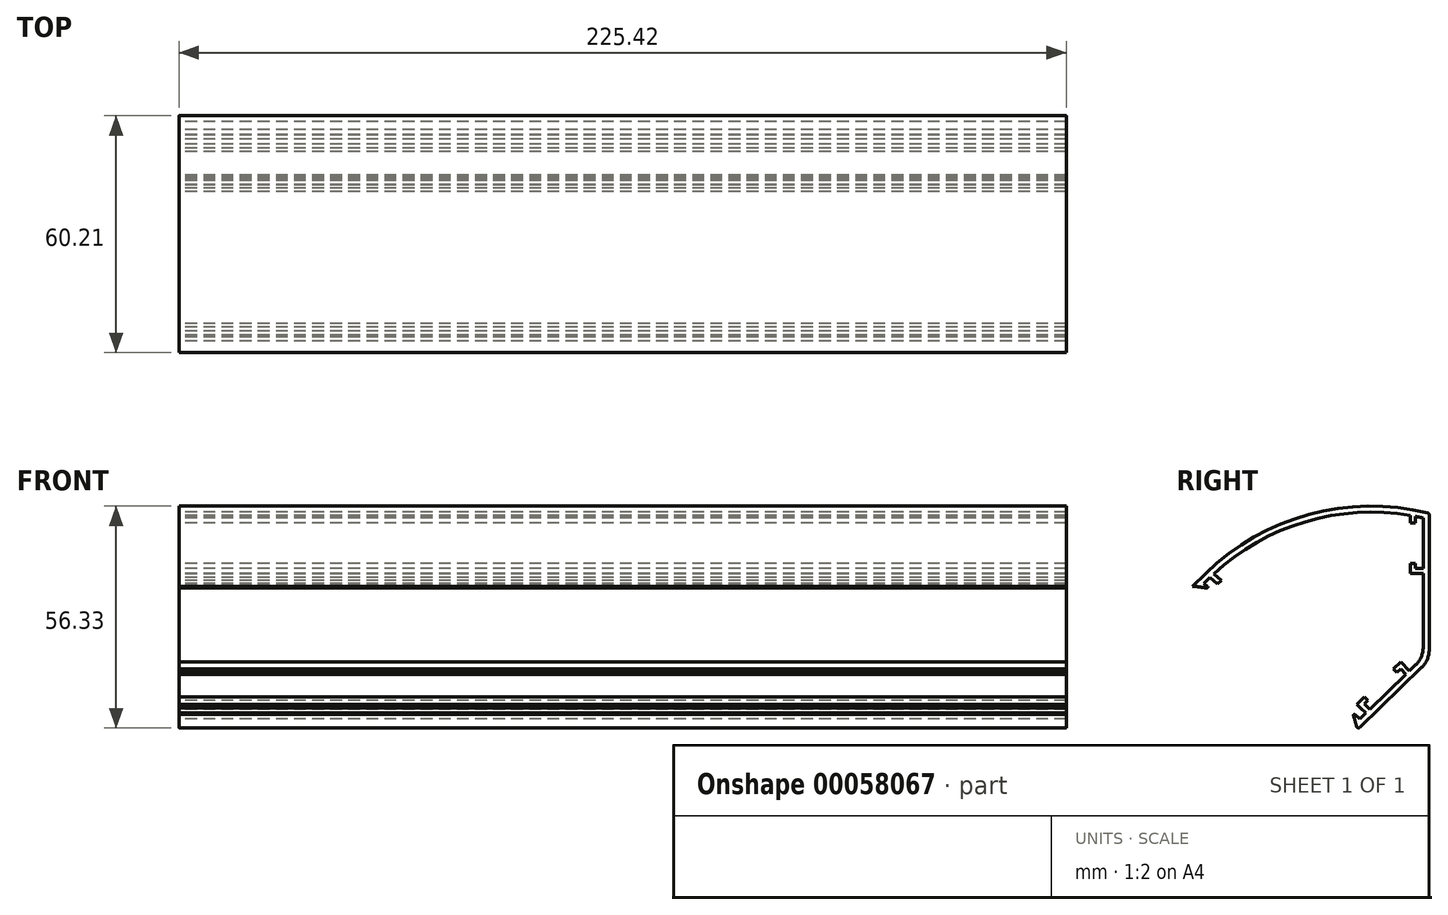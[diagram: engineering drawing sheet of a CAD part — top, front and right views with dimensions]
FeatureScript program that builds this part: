
annotation { "Feature Type Name" : "Feature", "Feature Type Description" : "" }
export const myFeature = defineFeature(function(context is Context, id is Id, definition is map)
    precondition{}
    {
        {
            var Q0;
            Q0=qCreatedBy(makeId("Right.planeOp"),FACE);
            var sketch = newSketch(context, id + "F0", { "sketchPlane" : qUnion([Q0])});
            skLineSegment(sketch, "E0", {"start": v(-18.27, -17.64) * mm, "end": v(0, 0) * mm});
            skLineSegment(sketch, "E1", {"start": v(0, 0) * mm, "end": v(0, 37.34) * mm});
            skArc(sketch, "E2", {"start": v(0, 37.34) * mm, "mid": v(-30.37, 37.1) * mm, "end": v(-56.79, 22.12) * mm});
            skLineSegment(sketch, "E3", {"start": v(-56.79, 22.12) * mm, "end": v(-60.2, 18.8) * mm});
            skLineSegment(sketch, "E4", {"start": v(-18.27, -17.64) * mm, "end": v(-60.2, 18.8) * mm});
            skLineSegment(sketch, "E5", {"start": v(-56.79, 22.12) * mm, "end": v(-18.27, -17.64) * mm, "construction": true});
            skLineSegment(sketch, "E6", {"start": v(0, 37.34) * mm, "end": v(-56.79, 22.12) * mm, "construction": true});
            skSolve(sketch);
        }
        {
            var Q0;
            Q0=qSketchRegion(id+"F0",true);
            extrude(context, id + "F1", {"entities" : qUnion([Q0]), "endBound" : BoundingType.SYMMETRIC, "depth" : 225.42 * mm});
        }
        {
            var Q0;
            Q0=makeQuery(id+"F1.opExtrude","SWEPT_FACE",FACE,{"disambiguationData":[OSD([sQuery(id+"F0.wireOp",EDGE,"E4")])]});
            var Q1;
            Q1=makeQuery(id+"F1.opExtrude","CAP_FACE",FACE,{"disambiguationData":[OSD([sQuery(id+"F0.wireOp",EDGE,"E0"),sQuery(id+"F0.wireOp",EDGE,"E1"),sQuery(id+"F0.wireOp",EDGE,"E2"),sQuery(id+"F0.wireOp",EDGE,"E3"),sQuery(id+"F0.wireOp",EDGE,"E4")])],"isStart":true});
            var Q2;
            Q2=makeQuery(id+"F1.opExtrude","CAP_FACE",FACE,{"disambiguationData":[OSD([sQuery(id+"F0.wireOp",EDGE,"E0"),sQuery(id+"F0.wireOp",EDGE,"E1"),sQuery(id+"F0.wireOp",EDGE,"E2"),sQuery(id+"F0.wireOp",EDGE,"E3"),sQuery(id+"F0.wireOp",EDGE,"E4")])],"isStart":false});
            shell(context, id + "F2", {"entities" : qUnion([Q0, Q1, Q2]), "thickness" : 1.52 * mm});
        }
        {
            var Q0;
            Q0=makeQuery(id+"F1.opExtrude","CAP_FACE",FACE,{"disambiguationData":[OSD([sQuery(id+"F0.wireOp",EDGE,"E0"),sQuery(id+"F0.wireOp",EDGE,"E1"),sQuery(id+"F0.wireOp",EDGE,"E2"),sQuery(id+"F0.wireOp",EDGE,"E3"),sQuery(id+"F0.wireOp",EDGE,"E4")])],"isStart":true});
            var sketch = newSketch(context, id + "F3", { "sketchPlane" : qUnion([Q0])});
            skLineSegment(sketch, "E7", {"start": v(60.2, 18.8) * mm, "end": v(18.27, -17.64) * mm, "construction": true});
            skSolve(sketch);
        }
        {
            var Q0;
            {var subQ6=sQuery(id+"F0.wireOp",EDGE,"E0");var subQ7=makeQuery(id+"F1.opExtrude","CAP_EDGE",EDGE,{"disambiguationData":[OSD([subQ6])],"isStart":true});Q0=makeQuery(id+"F3.imprint","IMPRINT",FACE,{"disambiguationData":[TD([[makeQuery(id+"F3.imprint","IMPRINT",EDGE,{"derivedFrom":subQ7}),-1.0]])]});}
            var sketch = newSketch(context, id + "F4", { "sketchPlane" : qUnion([Q0])});
            skLineSegment(sketch, "E8", {"start": v(59.05, 17.8) * mm, "end": v(57.23, 19.57) * mm});
            skLineSegment(sketch, "E9", {"start": v(57.23, 19.57) * mm, "end": v(55.31, 17.9) * mm});
            skLineSegment(sketch, "E10", {"start": v(55.31, 17.9) * mm, "end": v(57.13, 16.14) * mm});
            skLineSegment(sketch, "E11", {"start": v(57.13, 16.14) * mm, "end": v(59.05, 17.8) * mm});
            skSolve(sketch);
        }
        {
            var Q0;
            Q0=qSketchRegion(id+"F4",true);
            var Q1;
            Q1=makeQuery(id+"F1.opExtrude","CAP_FACE",FACE,{"disambiguationData":[OSD([sQuery(id+"F0.wireOp",EDGE,"E0"),sQuery(id+"F0.wireOp",EDGE,"E1"),sQuery(id+"F0.wireOp",EDGE,"E2"),sQuery(id+"F0.wireOp",EDGE,"E3"),sQuery(id+"F0.wireOp",EDGE,"E4")])],"isStart":false});
            extrude(context, id + "F5", {"entities" : qUnion([Q0]), "operationType" : NewBodyOperationType.ADD, "endBound" : BoundingType.UP_TO_SURFACE, "oppositeDirection" : true, "endBoundEntityFace" : qUnion([Q1]), "depth" : 25.4 * mm});
        }
        {
            var Q0;
            {var subQ6=sQuery(id+"F0.wireOp",EDGE,"E0");var subQ7=makeQuery(id+"F1.opExtrude","CAP_EDGE",EDGE,{"disambiguationData":[OSD([subQ6])],"isStart":true});Q0=makeQuery(id+"F3.imprint","IMPRINT",FACE,{"disambiguationData":[TD([[makeQuery(id+"F3.imprint","IMPRINT",EDGE,{"derivedFrom":subQ7}),-1.0]])]});}
            var sketch = newSketch(context, id + "F6", { "sketchPlane" : qUnion([Q0])});
            skLineSegment(sketch, "E12", {"start": v(17.6, -14.88) * mm, "end": v(19.43, -16.64) * mm});
            skLineSegment(sketch, "E13", {"start": v(19.43, -16.64) * mm, "end": v(21.34, -14.97) * mm});
            skLineSegment(sketch, "E14", {"start": v(21.34, -14.97) * mm, "end": v(19.52, -13.2) * mm});
            skLineSegment(sketch, "E15", {"start": v(19.52, -13.2) * mm, "end": v(17.6, -14.88) * mm});
            skSolve(sketch);
        }
        {
            var Q0;
            Q0=qSketchRegion(id+"F6",true);
            var Q1;
            Q1=makeQuery(id+"F5.boolean.opBoolean","MERGE",FACE,{"derivedFrom":[makeQuery(id+"F1.opExtrude","CAP_FACE",FACE,{"disambiguationData":[OSD([sQuery(id+"F0.wireOp",EDGE,"E0"),sQuery(id+"F0.wireOp",EDGE,"E1"),sQuery(id+"F0.wireOp",EDGE,"E2"),sQuery(id+"F0.wireOp",EDGE,"E3"),sQuery(id+"F0.wireOp",EDGE,"E4")])],"isStart":false}),makeQuery(id+"F5.opExtrude","CAP_FACE",FACE,{"disambiguationData":[OSD([sQuery(id+"F4.wireOp",EDGE,"E8"),sQuery(id+"F4.wireOp",EDGE,"E9"),sQuery(id+"F4.wireOp",EDGE,"E10"),sQuery(id+"F4.wireOp",EDGE,"E11")])],"isStart":false})]});
            extrude(context, id + "F7", {"entities" : qUnion([Q0]), "operationType" : NewBodyOperationType.ADD, "endBound" : BoundingType.UP_TO_SURFACE, "oppositeDirection" : true, "endBoundEntityFace" : qUnion([Q1]), "depth" : 25.4 * mm});
        }
        {
            var Q0;
            {var subQ6=sQuery(id+"F0.wireOp",EDGE,"E0");var subQ7=makeQuery(id+"F1.opExtrude","CAP_EDGE",EDGE,{"disambiguationData":[OSD([subQ6])],"isStart":true});Q0=makeQuery(id+"F3.imprint","IMPRINT",FACE,{"disambiguationData":[TD([[makeQuery(id+"F3.imprint","IMPRINT",EDGE,{"derivedFrom":subQ7}),-1.0]])]});}
            var sketch = newSketch(context, id + "F8", { "sketchPlane" : qUnion([Q0])});
            skCircle(sketch, "E16", {"center": v(64.21, -28.14) * mm, "radius": 47.12 * mm});
            skSolve(sketch);
        }
        {
            var Q0;
            Q0=qSketchRegion(id+"F8",true);
            var Q1;
            Q1=makeQuery(id+"F7.boolean.opBoolean","MERGE",FACE,{"derivedFrom":[makeQuery(id+"F5.boolean.opBoolean","MERGE",FACE,{"derivedFrom":[makeQuery(id+"F1.opExtrude","CAP_FACE",FACE,{"disambiguationData":[OSD([sQuery(id+"F0.wireOp",EDGE,"E0"),sQuery(id+"F0.wireOp",EDGE,"E1"),sQuery(id+"F0.wireOp",EDGE,"E2"),sQuery(id+"F0.wireOp",EDGE,"E3"),sQuery(id+"F0.wireOp",EDGE,"E4")])],"isStart":false}),makeQuery(id+"F5.opExtrude","CAP_FACE",FACE,{"disambiguationData":[OSD([sQuery(id+"F4.wireOp",EDGE,"E8"),sQuery(id+"F4.wireOp",EDGE,"E9"),sQuery(id+"F4.wireOp",EDGE,"E10"),sQuery(id+"F4.wireOp",EDGE,"E11")])],"isStart":false})]}),makeQuery(id+"F7.opExtrude","CAP_FACE",FACE,{"disambiguationData":[OSD([sQuery(id+"F6.wireOp",EDGE,"E12"),sQuery(id+"F6.wireOp",EDGE,"E13"),sQuery(id+"F6.wireOp",EDGE,"E14"),sQuery(id+"F6.wireOp",EDGE,"E15")])],"isStart":false})]});
            extrude(context, id + "F9", {"entities" : qUnion([Q0]), "operationType" : NewBodyOperationType.REMOVE, "endBound" : BoundingType.UP_TO_SURFACE, "oppositeDirection" : true, "endBoundEntityFace" : qUnion([Q1]), "depth" : 25.4 * mm});
        }
        {
            var Q0;
            {var subQ6=sQuery(id+"F0.wireOp",EDGE,"E0");var subQ7=makeQuery(id+"F1.opExtrude","CAP_EDGE",EDGE,{"disambiguationData":[OSD([subQ6])],"isStart":true});Q0=makeQuery(id+"F3.imprint","IMPRINT",FACE,{"disambiguationData":[TD([[makeQuery(id+"F3.imprint","IMPRINT",EDGE,{"derivedFrom":subQ7}),-1.0]])]});}
            var sketch = newSketch(context, id + "F10", { "sketchPlane" : qUnion([Q0])});
            skLineSegment(sketch, "E17", {"start": v(16.05, -13.38) * mm, "end": v(17.53, -12.09) * mm});
            skLineSegment(sketch, "E18", {"start": v(17.53, -12.09) * mm, "end": v(16.5, -11.09) * mm});
            skLineSegment(sketch, "E19", {"start": v(16.5, -11.09) * mm, "end": v(15.13, -12.5) * mm});
            skLineSegment(sketch, "E20", {"start": v(15.13, -12.5) * mm, "end": v(16.05, -13.38) * mm});
            skSolve(sketch);
        }
        {
            var Q0;
            {var subQ6=sQuery(id+"F0.wireOp",EDGE,"E0");var subQ7=makeQuery(id+"F1.opExtrude","CAP_EDGE",EDGE,{"disambiguationData":[OSD([subQ6])],"isStart":true});Q0=makeQuery(id+"F3.imprint","IMPRINT",FACE,{"disambiguationData":[TD([[makeQuery(id+"F3.imprint","IMPRINT",EDGE,{"derivedFrom":subQ7}),-1.0]])]});}
            var sketch = newSketch(context, id + "F11", { "sketchPlane" : qUnion([Q0])});
            skLineSegment(sketch, "E21", {"start": v(17.53, -12.09) * mm, "end": v(15.58, -10.2) * mm});
            skLineSegment(sketch, "E22", {"start": v(15.58, -10.2) * mm, "end": v(16.46, -9.3) * mm});
            skLineSegment(sketch, "E23", {"start": v(16.46, -9.3) * mm, "end": v(18.4, -11.17) * mm});
            skLineSegment(sketch, "E24", {"start": v(18.4, -11.17) * mm, "end": v(17.53, -12.09) * mm});
            skSolve(sketch);
        }
        {
            var Q0;
            {var subQ6=sQuery(id+"F0.wireOp",EDGE,"E0");var subQ7=makeQuery(id+"F1.opExtrude","CAP_EDGE",EDGE,{"disambiguationData":[OSD([subQ6])],"isStart":true});Q0=makeQuery(id+"F3.imprint","IMPRINT",FACE,{"disambiguationData":[TD([[makeQuery(id+"F3.imprint","IMPRINT",EDGE,{"derivedFrom":subQ7}),-1.0]])]});}
            var sketch = newSketch(context, id + "F12", { "sketchPlane" : qUnion([Q0])});
            skLineSegment(sketch, "E25", {"start": v(55.68, 21.07) * mm, "end": v(53.76, 19.4) * mm});
            skLineSegment(sketch, "E26", {"start": v(53.76, 19.4) * mm, "end": v(52.85, 20.3) * mm});
            skLineSegment(sketch, "E27", {"start": v(52.85, 20.3) * mm, "end": v(54.76, 21.96) * mm});
            skLineSegment(sketch, "E28", {"start": v(54.76, 21.96) * mm, "end": v(55.68, 21.07) * mm});
            skSolve(sketch);
        }
        {
            var Q0;
            {var subQ6=sQuery(id+"F0.wireOp",EDGE,"E0");var subQ7=makeQuery(id+"F1.opExtrude","CAP_EDGE",EDGE,{"disambiguationData":[OSD([subQ6])],"isStart":true});Q0=makeQuery(id+"F3.imprint","IMPRINT",FACE,{"disambiguationData":[TD([[makeQuery(id+"F3.imprint","IMPRINT",EDGE,{"derivedFrom":subQ7}),-1.0]])]});}
            var sketch = newSketch(context, id + "F13", { "sketchPlane" : qUnion([Q0])});
            skLineSegment(sketch, "E29", {"start": v(5.9, -3.58) * mm, "end": v(7.26, -2.18) * mm});
            skLineSegment(sketch, "E30", {"start": v(7.26, -2.18) * mm, "end": v(8.18, -3.06) * mm});
            skLineSegment(sketch, "E31", {"start": v(8.18, -3.06) * mm, "end": v(9.06, -2.15) * mm});
            skLineSegment(sketch, "E32", {"start": v(9.06, -2.15) * mm, "end": v(7.23, -0.38) * mm});
            skLineSegment(sketch, "E33", {"start": v(7.23, -0.38) * mm, "end": v(5, -2.7) * mm});
            skLineSegment(sketch, "E34", {"start": v(5, -2.7) * mm, "end": v(5.9, -3.58) * mm});
            skSolve(sketch);
        }
        {
            var Q0;
            {var subQ6=sQuery(id+"F12.wireOp",EDGE,"E28");Q0=makeQuery(id+"F12.imprint","IMPRINT",FACE,{"disambiguationData":[TD([[makeQuery(id+"F12.imprint","IMPRINT",EDGE,{"derivedFrom":subQ6}),1.0]])]});}
            var sketch = newSketch(context, id + "F14", { "sketchPlane" : qUnion([Q0])});
            skLineSegment(sketch, "E35", {"start": v(1.52, 22.04) * mm, "end": v(1.52, 23.3) * mm});
            skLineSegment(sketch, "E36", {"start": v(1.52, 23.3) * mm, "end": v(3.48, 23.3) * mm});
            skLineSegment(sketch, "E37", {"start": v(3.48, 23.3) * mm, "end": v(3.48, 24.58) * mm});
            skLineSegment(sketch, "E38", {"start": v(3.48, 24.58) * mm, "end": v(4.75, 24.58) * mm});
            skLineSegment(sketch, "E39", {"start": v(4.75, 24.58) * mm, "end": v(4.75, 22.04) * mm});
            skLineSegment(sketch, "E40", {"start": v(4.75, 22.04) * mm, "end": v(1.52, 22.04) * mm});
            skLineSegment(sketch, "E41", {"start": v(3.48, 36.78) * mm, "end": v(3.48, 34.87) * mm});
            skLineSegment(sketch, "E42", {"start": v(3.48, 34.87) * mm, "end": v(4.75, 34.87) * mm});
            skLineSegment(sketch, "E43", {"start": v(4.75, 34.87) * mm, "end": v(4.75, 36.78) * mm});
            skLineSegment(sketch, "E44", {"start": v(4.75, 36.78) * mm, "end": v(3.48, 36.78) * mm});
            skSolve(sketch);
        }
        {
            var Q0;
            Q0=qSketchRegion(id+"F10",true);
            var Q1;
            Q1=qSketchRegion(id+"F11",true);
            var Q2;
            Q2=qSketchRegion(id+"F12",true);
            var Q3;
            Q3=qSketchRegion(id+"F13",true);
            var Q4;
            Q4=qSketchRegion(id+"F14",true);
            var Q5;
            Q5=makeQuery(id+"F7.boolean.opBoolean","MERGE",FACE,{"derivedFrom":[makeQuery(id+"F5.boolean.opBoolean","MERGE",FACE,{"derivedFrom":[makeQuery(id+"F1.opExtrude","CAP_FACE",FACE,{"disambiguationData":[OSD([sQuery(id+"F0.wireOp",EDGE,"E0"),sQuery(id+"F0.wireOp",EDGE,"E1"),sQuery(id+"F0.wireOp",EDGE,"E2"),sQuery(id+"F0.wireOp",EDGE,"E3"),sQuery(id+"F0.wireOp",EDGE,"E4")])],"isStart":false}),makeQuery(id+"F5.opExtrude","CAP_FACE",FACE,{"disambiguationData":[OSD([sQuery(id+"F4.wireOp",EDGE,"E8"),sQuery(id+"F4.wireOp",EDGE,"E9"),sQuery(id+"F4.wireOp",EDGE,"E10"),sQuery(id+"F4.wireOp",EDGE,"E11")])],"isStart":false})]}),makeQuery(id+"F7.opExtrude","CAP_FACE",FACE,{"disambiguationData":[OSD([sQuery(id+"F6.wireOp",EDGE,"E12"),sQuery(id+"F6.wireOp",EDGE,"E13"),sQuery(id+"F6.wireOp",EDGE,"E14"),sQuery(id+"F6.wireOp",EDGE,"E15")])],"isStart":false})]});
            extrude(context, id + "F15", {"entities" : qUnion([Q0, Q1, Q2, Q3, Q4]), "operationType" : NewBodyOperationType.ADD, "endBound" : BoundingType.UP_TO_SURFACE, "oppositeDirection" : true, "endBoundEntityFace" : qUnion([Q5]), "depth" : 25.4 * mm});
        }
        {
            var Q0;
            Q0=makeQuery(id+"F1.opExtrude","SWEPT_EDGE",EDGE,{"disambiguationData":[OSD([sQuery(id+"F0.wireOp",EDGE,"E0"),sQuery(id+"F0.wireOp",EDGE,"E4")])]});
            var Q1;
            Q1=makeQuery(id+"F1.opExtrude","SWEPT_EDGE",EDGE,{"disambiguationData":[OSD([sQuery(id+"F0.wireOp",EDGE,"E3"),sQuery(id+"F0.wireOp",EDGE,"E4")])]});
            var Q2;
            Q2=makeQuery(id+"F1.opExtrude","SWEPT_EDGE",EDGE,{"disambiguationData":[OSD([sQuery(id+"F0.wireOp",EDGE,"E1"),sQuery(id+"F0.wireOp",EDGE,"E2")])]});
            fillet(context, id + "F16", {"entities" : qUnion([Q0, Q1, Q2]), "radius" : 0.5 * mm, "allowEdgeOverflow" : false});
        }
        {
            var Q0;
            Q0=makeQuery(id+"F2.opShell","OFFSET_EDGE",EDGE,{"disambiguationData":[OSD([sQuery(id+"F0.wireOp",EDGE,"E0"),sQuery(id+"F0.wireOp",EDGE,"E1")])]});
            var Q1;
            Q1=makeQuery(id+"F1.opExtrude","SWEPT_EDGE",EDGE,{"disambiguationData":[OSD([sQuery(id+"F0.wireOp",EDGE,"E0"),sQuery(id+"F0.wireOp",EDGE,"E1")])]});
            fillet(context, id + "F17", {"entities" : qUnion([Q0, Q1]), "radius" : 6.35 * mm, "tangentPropagation" : true, "allowEdgeOverflow" : false});
        }
        {
            var Q0;
            Q0=makeQuery(id+"F7.opExtrude","SWEPT_EDGE",EDGE,{"disambiguationData":[OSD([sQuery(id+"F6.wireOp",EDGE,"E14"),sQuery(id+"F6.wireOp",EDGE,"E15")])]});
            var Q1;
            Q1=makeQuery(id+"F9.boolean.opBoolean","INTERSECT",EDGE,{"derivedFrom":[makeQuery(id+"F5.opExtrude","SWEPT_FACE",FACE,{"disambiguationData":[OSD([sQuery(id+"F4.wireOp",EDGE,"E9")])]}),makeQuery(id+"F9.opExtrude","SWEPT_FACE",FACE,{"disambiguationData":[OSD([sQuery(id+"F8.wireOp",EDGE,"E16")])]})]});
            fillet(context, id + "F18", {"entities" : qUnion([Q0, Q1]), "radius" : 0.25 * mm, "tangentPropagation" : true, "allowEdgeOverflow" : false});
        }
    });
